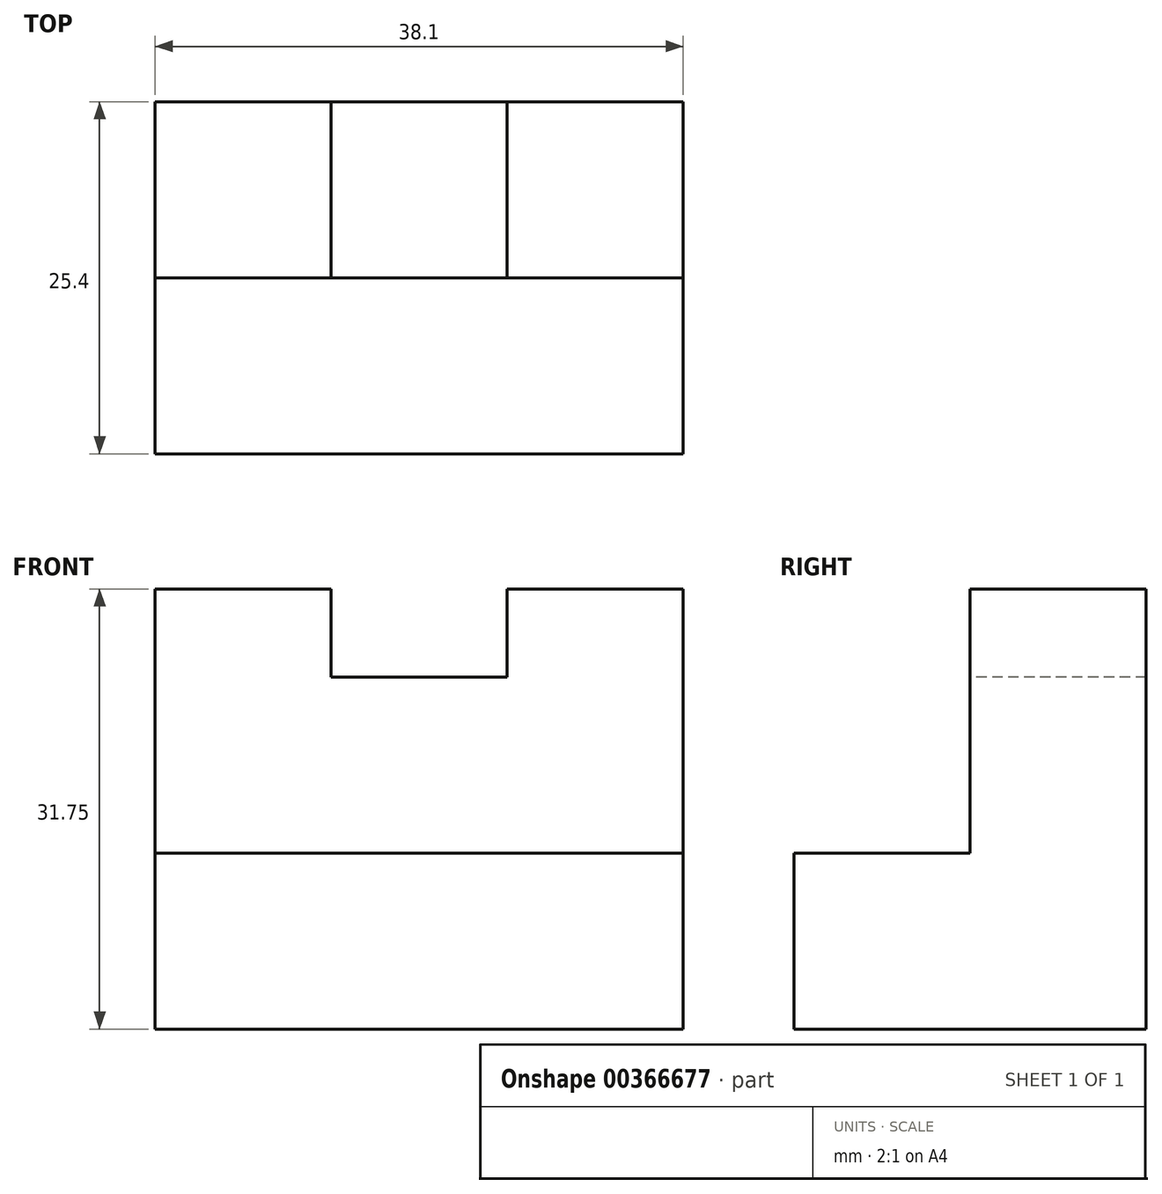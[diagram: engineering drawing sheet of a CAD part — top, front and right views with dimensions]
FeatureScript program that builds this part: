
annotation { "Feature Type Name" : "Feature", "Feature Type Description" : "" }
export const myFeature = defineFeature(function(context is Context, id is Id, definition is map)
    precondition{}
    {
        {
            var Q0;
            Q0=qCreatedBy(makeId("Front.planeOp"),FACE);
            var sketch = newSketch(context, id + "F0", { "sketchPlane" : qUnion([Q0])});
            skLineSegment(sketch, "E0", {"start": v(-55.52, 0) * mm, "end": v(-55.52, 31.75) * mm});
            skLineSegment(sketch, "E1", {"start": v(-55.52, 31.75) * mm, "end": v(-17.42, 31.75) * mm});
            skLineSegment(sketch, "E2", {"start": v(-17.42, 31.75) * mm, "end": v(-17.42, 0) * mm});
            skLineSegment(sketch, "E3", {"start": v(-17.42, 0) * mm, "end": v(-55.52, 0) * mm});
            skSolve(sketch);
        }
        {
            var Q0;
            Q0=makeQuery(id+"F0.imprint","IMPRINT",FACE,{"disambiguationData":[TD([[makeQuery(id+"F0.imprint","IMPRINT",EDGE,{"derivedFrom":sQuery(id+"F0.wireOp",EDGE,"E0")}),-1.0]])]});
            extrude(context, id + "F1", {"entities" : qUnion([Q0]), "depth" : 25.4 * mm});
        }
        {
            var Q0;
            Q0=makeQuery(id+"F1.opExtrude","CAP_FACE",FACE,{"disambiguationData":[OSD([sQuery(id+"F0.wireOp",EDGE,"E0"),sQuery(id+"F0.wireOp",EDGE,"E1"),sQuery(id+"F0.wireOp",EDGE,"E2"),sQuery(id+"F0.wireOp",EDGE,"E3")])],"isStart":false});
            var sketch = newSketch(context, id + "F2", { "sketchPlane" : qUnion([Q0])});
            skLineSegment(sketch, "E4", {"start": v(-55.52, 12.7) * mm, "end": v(-17.42, 12.7) * mm});
            skSolve(sketch);
        }
        {
            var Q0;
            {var subQ0=sQuery(id+"F2.wireOp",EDGE,"E4");Q0=makeQuery(id+"F2.imprint","IMPRINT",FACE,{"disambiguationData":[TD([[makeQuery(id+"F2.imprint","IMPRINT",EDGE,{"derivedFrom":subQ0}),1.0]])]});}
            extrude(context, id + "F3", {"entities" : qUnion([Q0]), "operationType" : NewBodyOperationType.REMOVE, "oppositeDirection" : true, "depth" : 12.7 * mm});
        }
        {
            var Q0;
            Q0=makeQuery(id+"F1.opExtrude","SWEPT_FACE",FACE,{"disambiguationData":[OSD([sQuery(id+"F0.wireOp",EDGE,"E1")])]});
            var sketch = newSketch(context, id + "F4", { "sketchPlane" : qUnion([Q0])});
            skLineSegment(sketch, "E5", {"start": v(-42.82, 0) * mm, "end": v(-42.82, -12.7) * mm});
            skLineSegment(sketch, "E6", {"start": v(-30.12, 0) * mm, "end": v(-30.12, -12.7) * mm});
            skSolve(sketch);
        }
        {
            var Q0;
            {var subQ0=sQuery(id+"F4.wireOp",EDGE,"E5");Q0=makeQuery(id+"F4.imprint","IMPRINT",FACE,{"disambiguationData":[TD([[makeQuery(id+"F4.imprint","IMPRINT",EDGE,{"derivedFrom":subQ0}),1.0]])]});}
            extrude(context, id + "F5", {"entities" : qUnion([Q0]), "operationType" : NewBodyOperationType.REMOVE, "oppositeDirection" : true, "depth" : 6.35 * mm});
        }
    });
